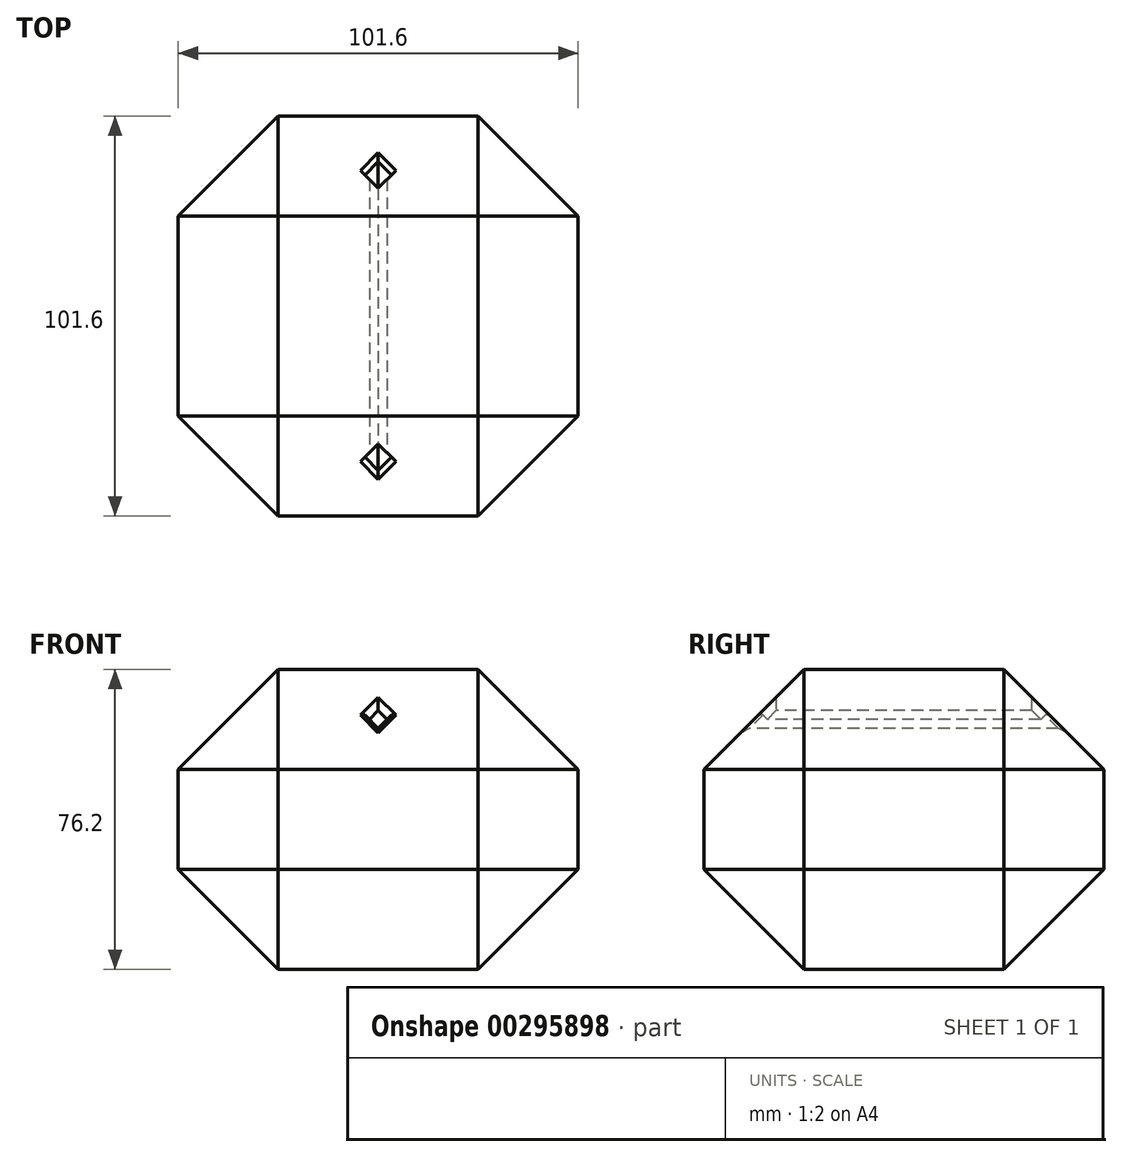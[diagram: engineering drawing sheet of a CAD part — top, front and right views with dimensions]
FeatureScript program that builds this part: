
annotation { "Feature Type Name" : "Feature", "Feature Type Description" : "" }
export const myFeature = defineFeature(function(context is Context, id is Id, definition is map)
    precondition{}
    {
        {
            var Q0;
            Q0=qCreatedBy(makeId("Front.planeOp"),FACE);
            var sketch = newSketch(context, id + "F0", { "sketchPlane" : qUnion([Q0])});
            skLineSegment(sketch, "E0.bottom", {"start": v(-50.8, -38.1) * mm, "end": v(50.8, -38.1) * mm});
            skLineSegment(sketch, "E0.top", {"start": v(-50.8, 38.1) * mm, "end": v(50.8, 38.1) * mm});
            skLineSegment(sketch, "E0.left", {"start": v(-50.8, -38.1) * mm, "end": v(-50.8, 38.1) * mm});
            skLineSegment(sketch, "E0.right", {"start": v(50.8, -38.1) * mm, "end": v(50.8, 38.1) * mm});
            skPoint(sketch, "E0.middle", {"position": v(0, 0) * mm});
            skSolve(sketch);
        }
        {
            var Q0;
            Q0=makeQuery(id+"F0.imprint","IMPRINT",FACE,{"disambiguationData":[TD([[makeQuery(id+"F0.imprint","IMPRINT",EDGE,{"derivedFrom":sQuery(id+"F0.wireOp",EDGE,"E0.bottom")}),1.0]])]});
            extrude(context, id + "F1", {"entities" : qUnion([Q0]), "endBound" : BoundingType.SYMMETRIC, "depth" : 101.6 * mm});
        }
        {
            var Q0;
            Q0=makeQuery(id+"F1.opExtrude","CAP_FACE",FACE,{"disambiguationData":[OSD([sQuery(id+"F0.wireOp",EDGE,"E0.bottom"),sQuery(id+"F0.wireOp",EDGE,"E0.top"),sQuery(id+"F0.wireOp",EDGE,"E0.left"),sQuery(id+"F0.wireOp",EDGE,"E0.right")])],"isStart":false});
            var Q1;
            Q1=makeQuery(id+"F1.opExtrude","SWEPT_FACE",FACE,{"disambiguationData":[OSD([sQuery(id+"F0.wireOp",EDGE,"E0.left")])]});
            var Q2;
            Q2=makeQuery(id+"F1.opExtrude","SWEPT_FACE",FACE,{"disambiguationData":[OSD([sQuery(id+"F0.wireOp",EDGE,"E0.bottom")])]});
            var Q3;
            Q3=makeQuery(id+"F1.opExtrude","SWEPT_FACE",FACE,{"disambiguationData":[OSD([sQuery(id+"F0.wireOp",EDGE,"E0.right")])]});
            var Q4;
            Q4=makeQuery(id+"F1.opExtrude","SWEPT_FACE",FACE,{"disambiguationData":[OSD([sQuery(id+"F0.wireOp",EDGE,"E0.top")])]});
            var Q5;
            Q5=makeQuery(id+"F1.opExtrude","CAP_FACE",FACE,{"disambiguationData":[OSD([sQuery(id+"F0.wireOp",EDGE,"E0.bottom"),sQuery(id+"F0.wireOp",EDGE,"E0.top"),sQuery(id+"F0.wireOp",EDGE,"E0.left"),sQuery(id+"F0.wireOp",EDGE,"E0.right")])],"isStart":true});
            chamfer(context, id + "F2", {"entities" : qUnion([Q0, Q1, Q2, Q3, Q4, Q5]), "width" : 25.4 * mm, "tangentPropagation" : true});
        }
        {
            var Q0;
            Q0=qCreatedBy(makeId("Front.planeOp"),FACE);
            var sketch = newSketch(context, id + "F3", { "sketchPlane" : qUnion([Q0])});
            skLineSegment(sketch, "E1.bottom", {"start": v(-2.25, 25.4) * mm, "end": v(0, 23.15) * mm});
            skLineSegment(sketch, "E1.top", {"start": v(0, 27.65) * mm, "end": v(2.25, 25.4) * mm});
            skLineSegment(sketch, "E1.left", {"start": v(-2.25, 25.4) * mm, "end": v(0, 27.65) * mm});
            skLineSegment(sketch, "E1.right", {"start": v(0, 23.15) * mm, "end": v(2.25, 25.4) * mm});
            skPoint(sketch, "E1.middle", {"position": v(0, 25.4) * mm});
            skSolve(sketch);
        }
        {
            var Q0;
            Q0 = qSketchRegion(id + "F3", true);
            extrude(context, id + "F4", {"entities" : qUnion([Q0]), "operationType" : NewBodyOperationType.REMOVE, "endBound" : BoundingType.SYMMETRIC, "oppositeDirection" : true, "depth" : 152.4 * mm});
        }
        {
            var Q0;
            {var subQ0=sQuery(id+"F0.wireOp",EDGE,"E0.top");Q0=makeQuery(id+"F4.boolean.opBoolean","INTERSECT",EDGE,{"derivedFrom":[makeQuery(id+"F2.opChamfer","BLEND_FACE",FACE,{"disambiguationData":[OSD([subQ0]),TDD([makeQuery(id+"F1.opExtrude","CAP_EDGE",EDGE,{"disambiguationData":[OSD([subQ0])],"isStart":false})])]}),makeQuery(id+"F4.opExtrude","SWEPT_FACE",FACE,{"disambiguationData":[OSD([sQuery(id+"F3.wireOp",EDGE,"E1.right")])]})]});}
            var Q1;
            {var subQ0=sQuery(id+"F0.wireOp",EDGE,"E0.top");Q1=makeQuery(id+"F4.boolean.opBoolean","INTERSECT",EDGE,{"derivedFrom":[makeQuery(id+"F2.opChamfer","BLEND_FACE",FACE,{"disambiguationData":[OSD([subQ0]),TDD([makeQuery(id+"F1.opExtrude","CAP_EDGE",EDGE,{"disambiguationData":[OSD([subQ0])],"isStart":false})])]}),makeQuery(id+"F4.opExtrude","SWEPT_FACE",FACE,{"disambiguationData":[OSD([sQuery(id+"F3.wireOp",EDGE,"E1.bottom")])]})]});}
            var Q2;
            {var subQ0=sQuery(id+"F0.wireOp",EDGE,"E0.top");Q2=makeQuery(id+"F4.boolean.opBoolean","INTERSECT",EDGE,{"derivedFrom":[makeQuery(id+"F2.opChamfer","BLEND_FACE",FACE,{"disambiguationData":[OSD([subQ0]),TDD([makeQuery(id+"F1.opExtrude","CAP_EDGE",EDGE,{"disambiguationData":[OSD([subQ0])],"isStart":true})])]}),makeQuery(id+"F4.opExtrude","SWEPT_FACE",FACE,{"disambiguationData":[OSD([sQuery(id+"F3.wireOp",EDGE,"E1.right")])]})]});}
            var Q3;
            {var subQ0=sQuery(id+"F0.wireOp",EDGE,"E0.top");Q3=makeQuery(id+"F4.boolean.opBoolean","INTERSECT",EDGE,{"derivedFrom":[makeQuery(id+"F2.opChamfer","BLEND_FACE",FACE,{"disambiguationData":[OSD([subQ0]),TDD([makeQuery(id+"F1.opExtrude","CAP_EDGE",EDGE,{"disambiguationData":[OSD([subQ0])],"isStart":true})])]}),makeQuery(id+"F4.opExtrude","SWEPT_FACE",FACE,{"disambiguationData":[OSD([sQuery(id+"F3.wireOp",EDGE,"E1.bottom")])]})]});}
            chamfer(context, id + "F5", {"entities" : qUnion([Q0, Q1, Q2, Q3]), "width" : 1.59 * mm, "tangentPropagation" : true});
        }
        {
            var Q0;
            {var subQ0=sQuery(id+"F0.wireOp",EDGE,"E0.top");Q0=makeQuery(id+"F4.boolean.opBoolean","INTERSECT",EDGE,{"derivedFrom":[makeQuery(id+"F2.opChamfer","BLEND_FACE",FACE,{"disambiguationData":[OSD([subQ0]),TDD([makeQuery(id+"F1.opExtrude","CAP_EDGE",EDGE,{"disambiguationData":[OSD([subQ0])],"isStart":false})])]}),makeQuery(id+"F4.opExtrude","SWEPT_FACE",FACE,{"disambiguationData":[OSD([sQuery(id+"F3.wireOp",EDGE,"E1.top")])]})]});}
            var Q1;
            {var subQ0=sQuery(id+"F0.wireOp",EDGE,"E0.top");Q1=makeQuery(id+"F4.boolean.opBoolean","INTERSECT",EDGE,{"derivedFrom":[makeQuery(id+"F2.opChamfer","BLEND_FACE",FACE,{"disambiguationData":[OSD([subQ0]),TDD([makeQuery(id+"F1.opExtrude","CAP_EDGE",EDGE,{"disambiguationData":[OSD([subQ0])],"isStart":false})])]}),makeQuery(id+"F4.opExtrude","SWEPT_FACE",FACE,{"disambiguationData":[OSD([sQuery(id+"F3.wireOp",EDGE,"E1.left")])]})]});}
            var Q2;
            {var subQ0=sQuery(id+"F0.wireOp",EDGE,"E0.top");Q2=makeQuery(id+"F4.boolean.opBoolean","INTERSECT",EDGE,{"derivedFrom":[makeQuery(id+"F2.opChamfer","BLEND_FACE",FACE,{"disambiguationData":[OSD([subQ0]),TDD([makeQuery(id+"F1.opExtrude","CAP_EDGE",EDGE,{"disambiguationData":[OSD([subQ0])],"isStart":true})])]}),makeQuery(id+"F4.opExtrude","SWEPT_FACE",FACE,{"disambiguationData":[OSD([sQuery(id+"F3.wireOp",EDGE,"E1.left")])]})]});}
            var Q3;
            {var subQ0=sQuery(id+"F0.wireOp",EDGE,"E0.top");Q3=makeQuery(id+"F4.boolean.opBoolean","INTERSECT",EDGE,{"derivedFrom":[makeQuery(id+"F2.opChamfer","BLEND_FACE",FACE,{"disambiguationData":[OSD([subQ0]),TDD([makeQuery(id+"F1.opExtrude","CAP_EDGE",EDGE,{"disambiguationData":[OSD([subQ0])],"isStart":true})])]}),makeQuery(id+"F4.opExtrude","SWEPT_FACE",FACE,{"disambiguationData":[OSD([sQuery(id+"F3.wireOp",EDGE,"E1.top")])]})]});}
            chamfer(context, id + "F6", {"entities" : qUnion([Q0, Q1, Q2, Q3]), "width" : 1.59 * mm, "tangentPropagation" : true});
        }
    });
